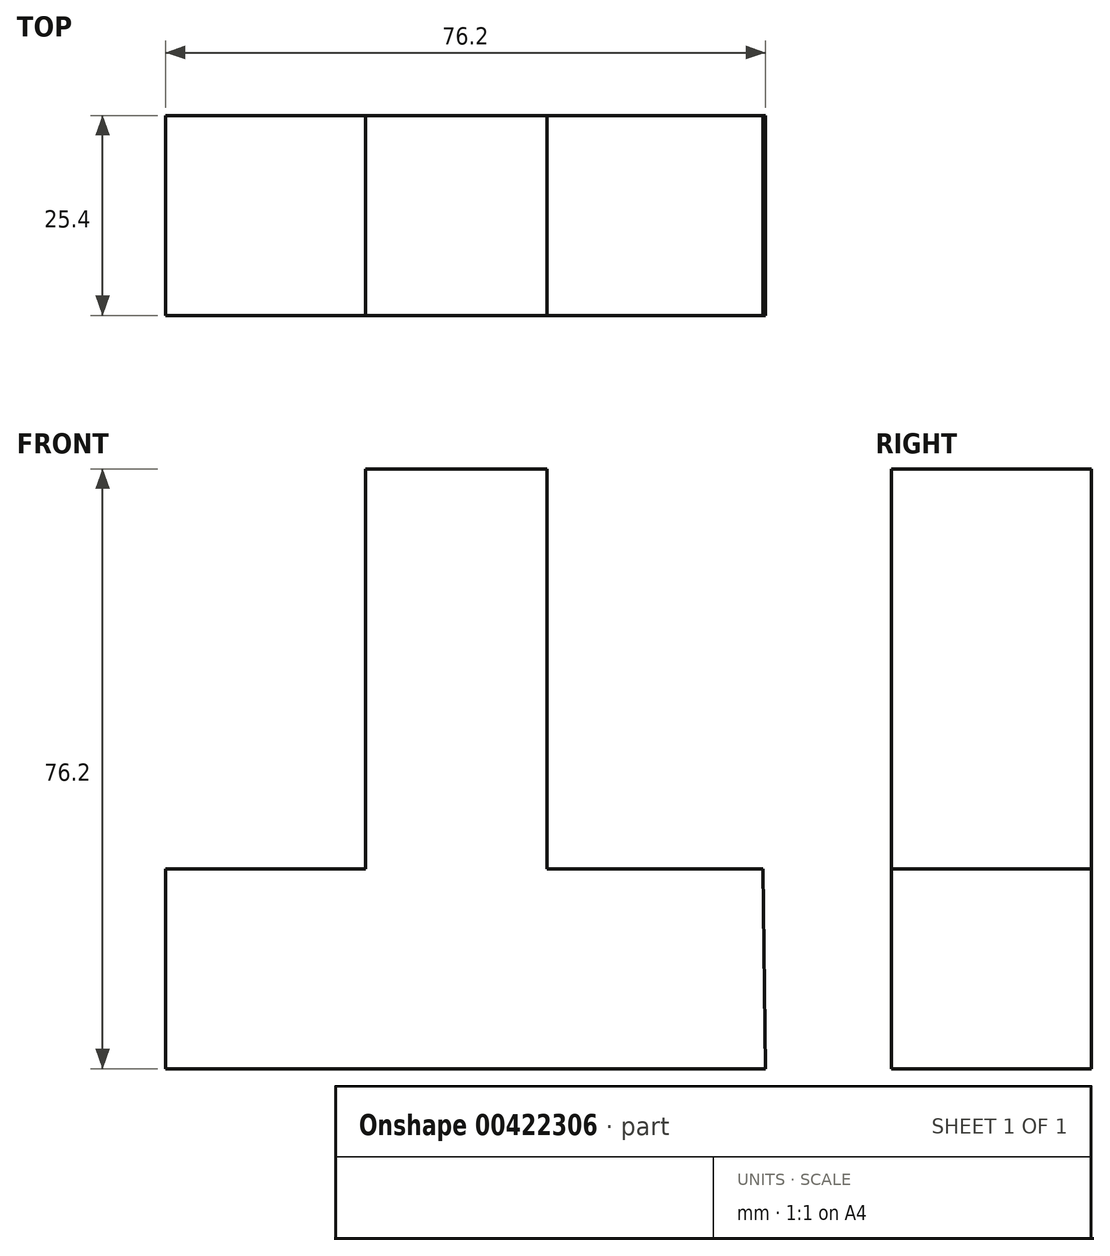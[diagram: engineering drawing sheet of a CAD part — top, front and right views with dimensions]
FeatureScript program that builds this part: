
annotation { "Feature Type Name" : "Feature", "Feature Type Description" : "" }
export const myFeature = defineFeature(function(context is Context, id is Id, definition is map)
    precondition{}
    {
        {
            var Q0;
            Q0=qCreatedBy(makeId("Front.planeOp"),FACE);
            var sketch = newSketch(context, id + "F0", { "sketchPlane" : qUnion([Q0])});
            skLineSegment(sketch, "E0", {"start": v(-48.47, -34.24) * mm, "end": v(27.73, -34.24) * mm});
            skLineSegment(sketch, "E1", {"start": v(-48.47, -34.24) * mm, "end": v(-48.47, -8.84) * mm});
            skLineSegment(sketch, "E2", {"start": v(-48.47, -8.84) * mm, "end": v(-23.07, -8.84) * mm});
            skLineSegment(sketch, "E3", {"start": v(-23.07, -8.84) * mm, "end": v(-23.07, 41.96) * mm});
            skLineSegment(sketch, "E4", {"start": v(-23.07, 41.96) * mm, "end": v(0, 41.96) * mm});
            skLineSegment(sketch, "E5", {"start": v(0, 41.96) * mm, "end": v(0, -8.84) * mm});
            skLineSegment(sketch, "E6", {"start": v(0, -8.84) * mm, "end": v(27.44, -8.84) * mm});
            skLineSegment(sketch, "E7", {"start": v(27.44, -8.84) * mm, "end": v(27.73, -34.24) * mm});
            skSolve(sketch);
        }
        {
            var Q0;
            Q0 = qSketchRegion(id + "F0", true);
            extrude(context, id + "F1", {"entities" : qUnion([Q0]), "depth" : 25.4 * mm});
        }
    });
